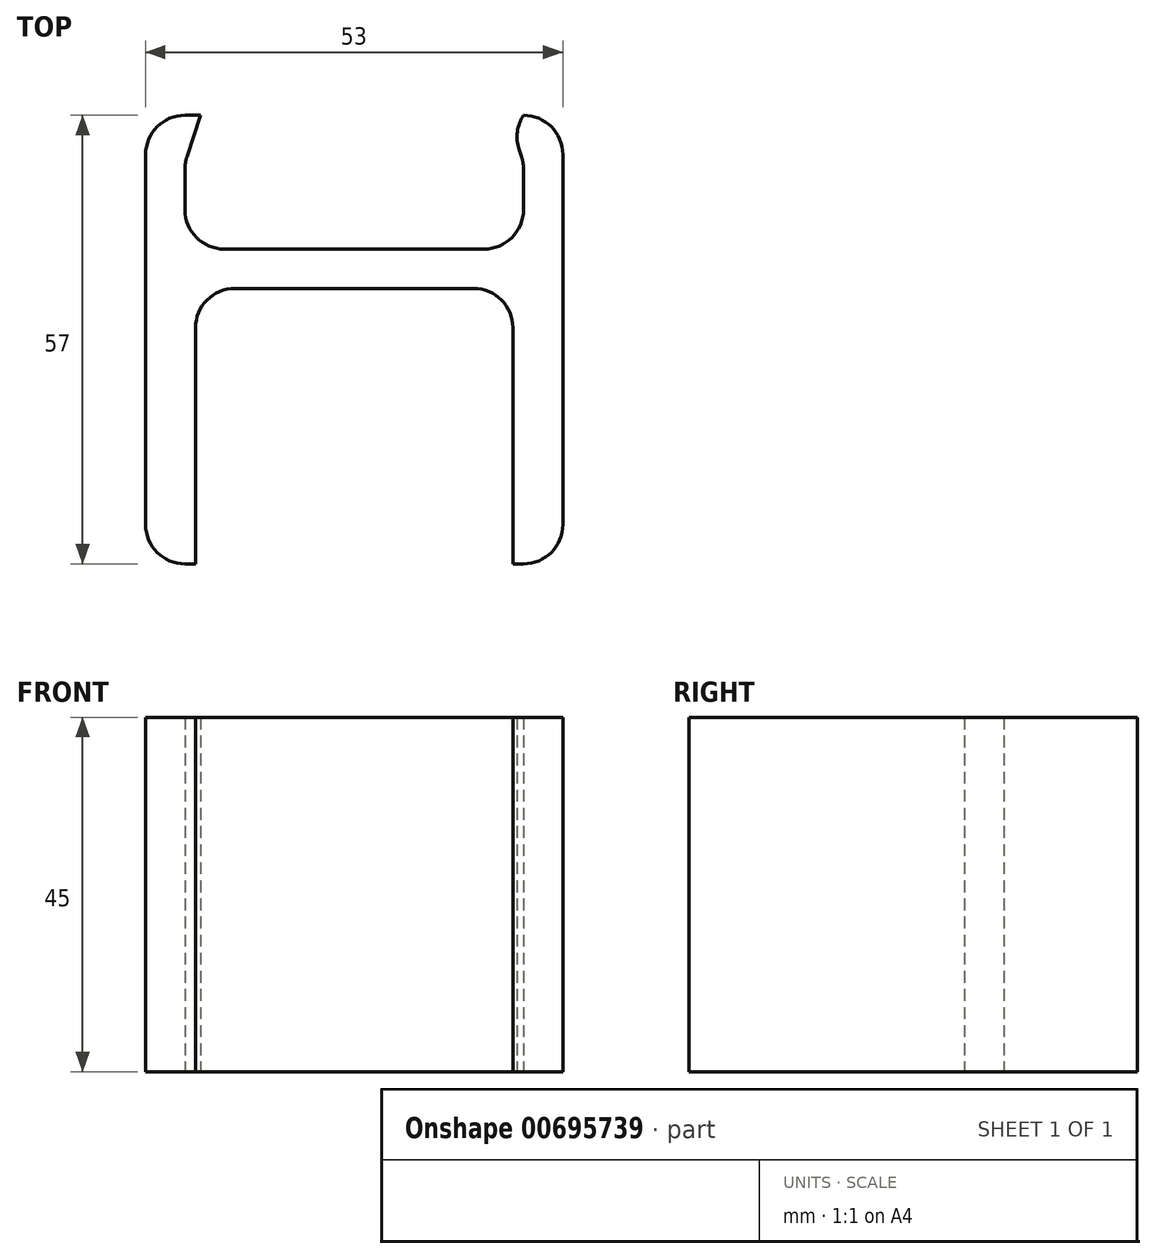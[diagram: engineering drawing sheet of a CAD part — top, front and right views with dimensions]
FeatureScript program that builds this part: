
annotation { "Feature Type Name" : "Feature", "Feature Type Description" : "" }
export const myFeature = defineFeature(function(context is Context, id is Id, definition is map)
    precondition{}
    {
        {
            var Q0;
            Q0=qCreatedBy(makeId("Top.planeOp"),FACE);
            var sketch = newSketch(context, id + "F0", { "sketchPlane" : qUnion([Q0])});
            skLineSegment(sketch, "E0", {"start": v(-20.15, -35) * mm, "end": v(-20.16, 0) * mm});
            skLineSegment(sketch, "E1", {"start": v(-20.16, 0) * mm, "end": v(20.15, 0) * mm});
            skLineSegment(sketch, "E2", {"start": v(20.15, 0) * mm, "end": v(20.16, -35) * mm});
            skLineSegment(sketch, "E3", {"start": v(21.5, 16) * mm, "end": v(21.5, 5) * mm});
            skLineSegment(sketch, "E4", {"start": v(21.5, 5) * mm, "end": v(-21.5, 5) * mm});
            skLineSegment(sketch, "E5", {"start": v(-21.5, 5) * mm, "end": v(-21.5, 16) * mm});
            skLineSegment(sketch, "E6", {"start": v(-26.5, 22) * mm, "end": v(-26.5, -35) * mm});
            skLineSegment(sketch, "E7", {"start": v(26.5, 22) * mm, "end": v(26.5, -35) * mm});
            skLineSegment(sketch, "E8", {"start": v(-21.5, 22) * mm, "end": v(-26.5, 22) * mm});
            skLineSegment(sketch, "E9", {"start": v(21.5, 22) * mm, "end": v(26.5, 22) * mm});
            skLineSegment(sketch, "E10", {"start": v(26.5, -35) * mm, "end": v(20.16, -35) * mm});
            skLineSegment(sketch, "E11", {"start": v(-20.15, -35) * mm, "end": v(-26.5, -35) * mm});
            skLineSegment(sketch, "E12", {"start": v(-21.5, 16) * mm, "end": v(-19.5, 22) * mm});
            skLineSegment(sketch, "E13", {"start": v(-19.5, 22) * mm, "end": v(-21.5, 22) * mm});
            skLineSegment(sketch, "E14.MirrorCS", {"start": v(19.5, 22) * mm, "end": v(21.5, 22) * mm});
            skLineSegment(sketch, "E15.MirrorCS", {"start": v(21.5, 16) * mm, "end": v(19.5, 22) * mm});
            skLineSegment(sketch, "E16.MirrorCS", {"start": v(21.5, 5) * mm, "end": v(21.5, 16) * mm});
            skSolve(sketch);
        }
        {
            var Q0;
            Q0 = qSketchRegion(id + "F0", true);
            extrude(context, id + "F1", {"entities" : qUnion([Q0]), "depth" : 45 * mm, "offsetDistance" : 25 * mm});
        }
        {
            var Q0;
            Q0=makeQuery(id+"F1.opExtrude","SWEPT_EDGE",EDGE,{"disambiguationData":[OSD([sQuery(id+"F0.wireOp",EDGE,"E10"),sQuery(id+"F0.wireOp",EDGE,"E7")])]});
            var Q1;
            Q1=makeQuery(id+"F1.opExtrude","SWEPT_EDGE",EDGE,{"disambiguationData":[OSD([sQuery(id+"F0.wireOp",EDGE,"E6"),sQuery(id+"F0.wireOp",EDGE,"E11")])]});
            var Q2;
            Q2=makeQuery(id+"F1.opExtrude","SWEPT_EDGE",EDGE,{"disambiguationData":[OSD([sQuery(id+"F0.wireOp",EDGE,"E6"),sQuery(id+"F0.wireOp",EDGE,"E8")])]});
            var Q3;
            Q3=makeQuery(id+"F1.opExtrude","SWEPT_EDGE",EDGE,{"disambiguationData":[OSD([sQuery(id+"F0.wireOp",EDGE,"E7"),sQuery(id+"F0.wireOp",EDGE,"E9")])]});
            fillet(context, id + "F2", {"entities" : qUnion([Q0, Q1, Q2, Q3]), "radius" : 5 * mm, "tangentPropagation" : true, "allowEdgeOverflow" : false});
        }
        {
            var Q0;
            Q0=makeQuery(id+"F1.opExtrude","SWEPT_EDGE",EDGE,{"disambiguationData":[OSD([sQuery(id+"F0.wireOp",EDGE,"E5"),sQuery(id+"F0.wireOp",EDGE,"E12")])]});
            var Q1;
            Q1=makeQuery(id+"F1.opExtrude","SWEPT_EDGE",EDGE,{"disambiguationData":[OSD([sQuery(id+"F0.wireOp",EDGE,"E15.MirrorCS"),sQuery(id+"F0.wireOp",EDGE,"E16.MirrorCS")])]});
            var Q2;
            Q2=makeQuery(id+"F1.opExtrude","SWEPT_EDGE",EDGE,{"disambiguationData":[OSD([sQuery(id+"F0.wireOp",EDGE,"E4"),sQuery(id+"F0.wireOp",EDGE,"E5")])]});
            var Q3;
            Q3=makeQuery(id+"F1.opExtrude","SWEPT_EDGE",EDGE,{"disambiguationData":[OSD([sQuery(id+"F0.wireOp",EDGE,"E4"),sQuery(id+"F0.wireOp",EDGE,"E16.MirrorCS")])]});
            fillet(context, id + "F3", {"entities" : qUnion([Q0, Q1, Q2, Q3]), "radius" : 5 * mm, "tangentPropagation" : true, "allowEdgeOverflow" : false});
        }
        {
            var Q0;
            Q0=makeQuery(id+"F1.opExtrude","SWEPT_EDGE",EDGE,{"disambiguationData":[OSD([sQuery(id+"F0.wireOp",EDGE,"E0"),sQuery(id+"F0.wireOp",EDGE,"E1")])]});
            var Q1;
            Q1=makeQuery(id+"F1.opExtrude","SWEPT_EDGE",EDGE,{"disambiguationData":[OSD([sQuery(id+"F0.wireOp",EDGE,"E1"),sQuery(id+"F0.wireOp",EDGE,"E2")])]});
            fillet(context, id + "F4", {"entities" : qUnion([Q0, Q1]), "radius" : 5 * mm, "tangentPropagation" : true, "allowEdgeOverflow" : false});
        }
    });
